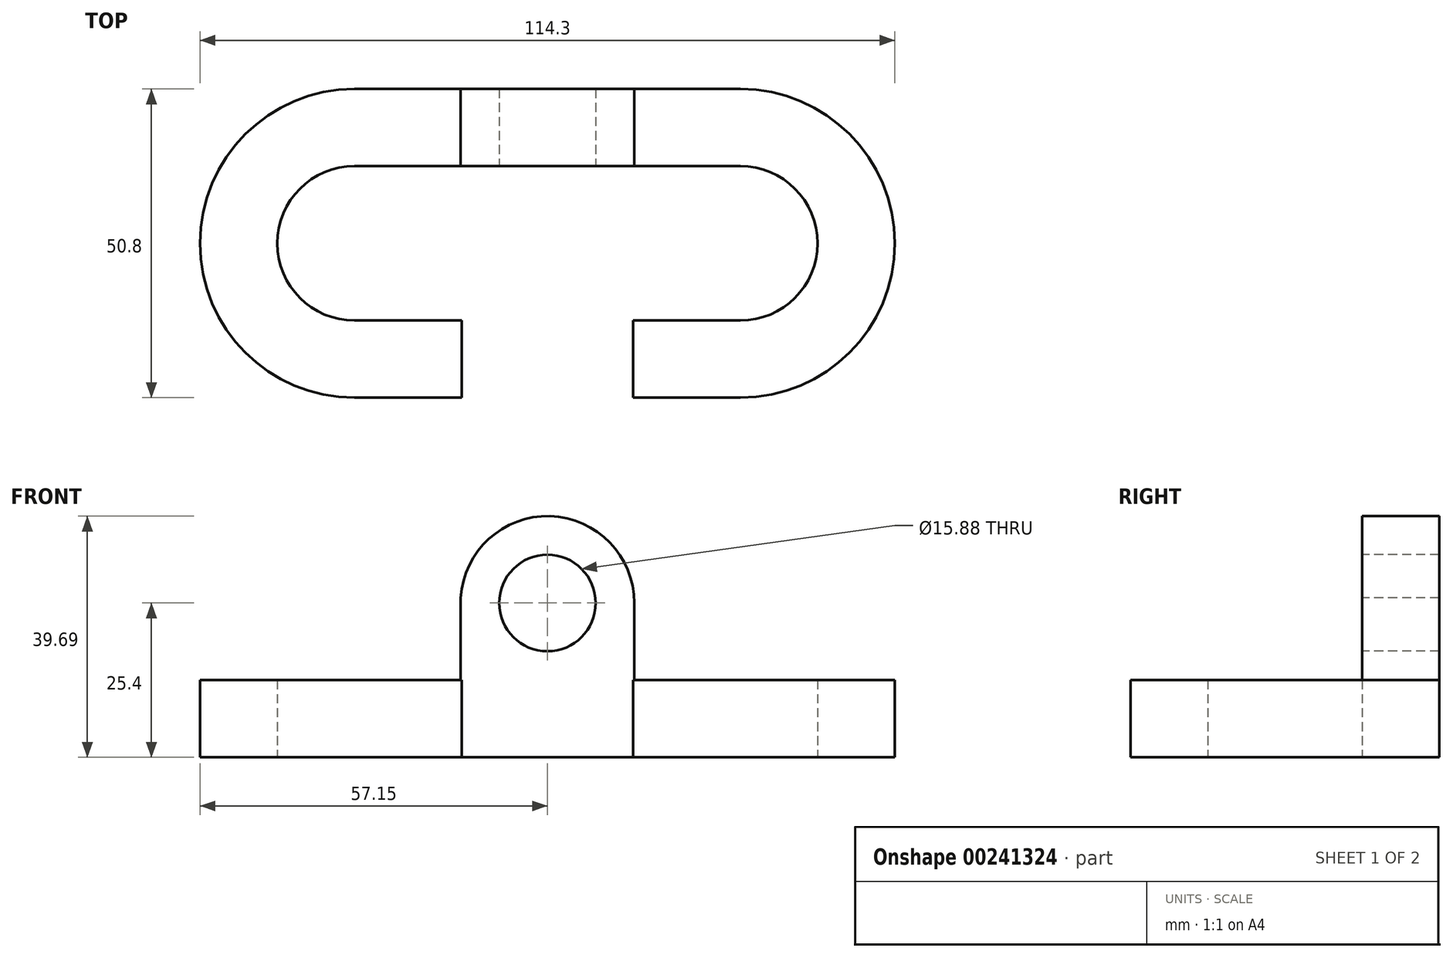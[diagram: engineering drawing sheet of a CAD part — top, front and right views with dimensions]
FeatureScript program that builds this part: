
annotation { "Feature Type Name" : "Feature", "Feature Type Description" : "" }
export const myFeature = defineFeature(function(context is Context, id is Id, definition is map)
    precondition{}
    {
        {
            var Q0;
            Q0=qCreatedBy(makeId("Top.planeOp"),FACE);
            var sketch = newSketch(context, id + "F0", { "sketchPlane" : qUnion([Q0])});
            skArc(sketch, "E0", {"start": v(31.75, -12.7) * mm, "mid": v(44.45, 0) * mm, "end": v(31.75, 12.7) * mm});
            skArc(sketch, "E1", {"start": v(31.75, -25.4) * mm, "mid": v(57.15, 0) * mm, "end": v(31.75, 25.4) * mm});
            skLineSegment(sketch, "E2", {"start": v(31.75, 25.4) * mm, "end": v(0, 25.4) * mm});
            skLineSegment(sketch, "E3", {"start": v(31.75, 12.7) * mm, "end": v(0, 12.7) * mm});
            skLineSegment(sketch, "E4", {"start": v(31.75, -12.7) * mm, "end": v(14.1, -12.7) * mm});
            skLineSegment(sketch, "E5", {"start": v(31.75, -25.4) * mm, "end": v(14.1, -25.4) * mm});
            skLineSegment(sketch, "E6", {"start": v(14.1, -12.7) * mm, "end": v(14.1, -25.4) * mm});
            skLineSegment(sketch, "E7.MirrorCS", {"start": v(-31.75, 25.4) * mm, "end": v(0, 25.4) * mm});
            skArc(sketch, "E8.MirrorCS", {"start": v(-31.75, -25.4) * mm, "mid": v(-57.15, 0) * mm, "end": v(-31.75, 25.4) * mm});
            skArc(sketch, "E9.MirrorCS", {"start": v(-31.75, -12.7) * mm, "mid": v(-44.45, 0) * mm, "end": v(-31.75, 12.7) * mm});
            skLineSegment(sketch, "E10.MirrorCS", {"start": v(-31.75, -12.7) * mm, "end": v(-14.1, -12.7) * mm});
            skLineSegment(sketch, "E11.MirrorCS", {"start": v(-31.75, -25.4) * mm, "end": v(-14.1, -25.4) * mm});
            skLineSegment(sketch, "E12.MirrorCS", {"start": v(-14.1, -12.7) * mm, "end": v(-14.1, -25.4) * mm});
            skLineSegment(sketch, "E13.MirrorCS", {"start": v(-31.75, 12.7) * mm, "end": v(0, 12.7) * mm});
            skSolve(sketch);
        }
        {
            var Q0;
            Q0=makeQuery(id+"F0.imprint","IMPRINT",FACE,{"disambiguationData":[TD([[makeQuery(id+"F0.imprint","IMPRINT",EDGE,{"derivedFrom":sQuery(id+"F0.wireOp",EDGE,"E0")}),-1.0]])]});
            extrude(context, id + "F1", {"entities" : qUnion([Q0]), "depth" : 12.7 * mm});
        }
        {
            var Q0;
            Q0=makeQuery(id+"F1.opExtrude","SWEPT_FACE",FACE,{"disambiguationData":[OSD([sQuery(id+"F0.wireOp",EDGE,"E3"),sQuery(id+"F0.wireOp",EDGE,"E13.MirrorCS")])]});
            var sketch = newSketch(context, id + "F2", { "sketchPlane" : qUnion([Q0])});
            skCircle(sketch, "E14", {"center": v(0, 25.4) * mm, "radius": 7.94 * mm});
            skArc(sketch, "E15", {"start": v(14.29, 25.4) * mm, "mid": v(0.44, 39.68) * mm, "end": v(-14.26, 26.28) * mm});
            skLineSegment(sketch, "E16", {"start": v(14.29, 25.4) * mm, "end": v(14.29, 25.4) * mm});
            skPoint(sketch, "E17.end.orphan", {"position": v(4.4, 26.28) * mm});
            skLineSegment(sketch, "E18", {"start": v(-14.26, 26.28) * mm, "end": v(-14.26, 0) * mm});
            skPoint(sketch, "E19.end.orphan", {"position": v(14.29, 0) * mm});
            skLineSegment(sketch, "E20", {"start": v(14.29, 25.4) * mm, "end": v(14.29, 12.7) * mm});
            skSolve(sketch);
        }
        {
            var Q0;
            Q0=makeQuery(id+"F2.imprint","IMPRINT",FACE,{"disambiguationData":[TD([[makeQuery(id+"F2.imprint","IMPRINT",EDGE,{"derivedFrom":sQuery(id+"F2.wireOp",EDGE,"E14")}),-1.0]])]});
            extrude(context, id + "F3", {"entities" : qUnion([Q0]), "operationType" : NewBodyOperationType.ADD, "oppositeDirection" : true, "depth" : 12.7 * mm});
        }
    });
